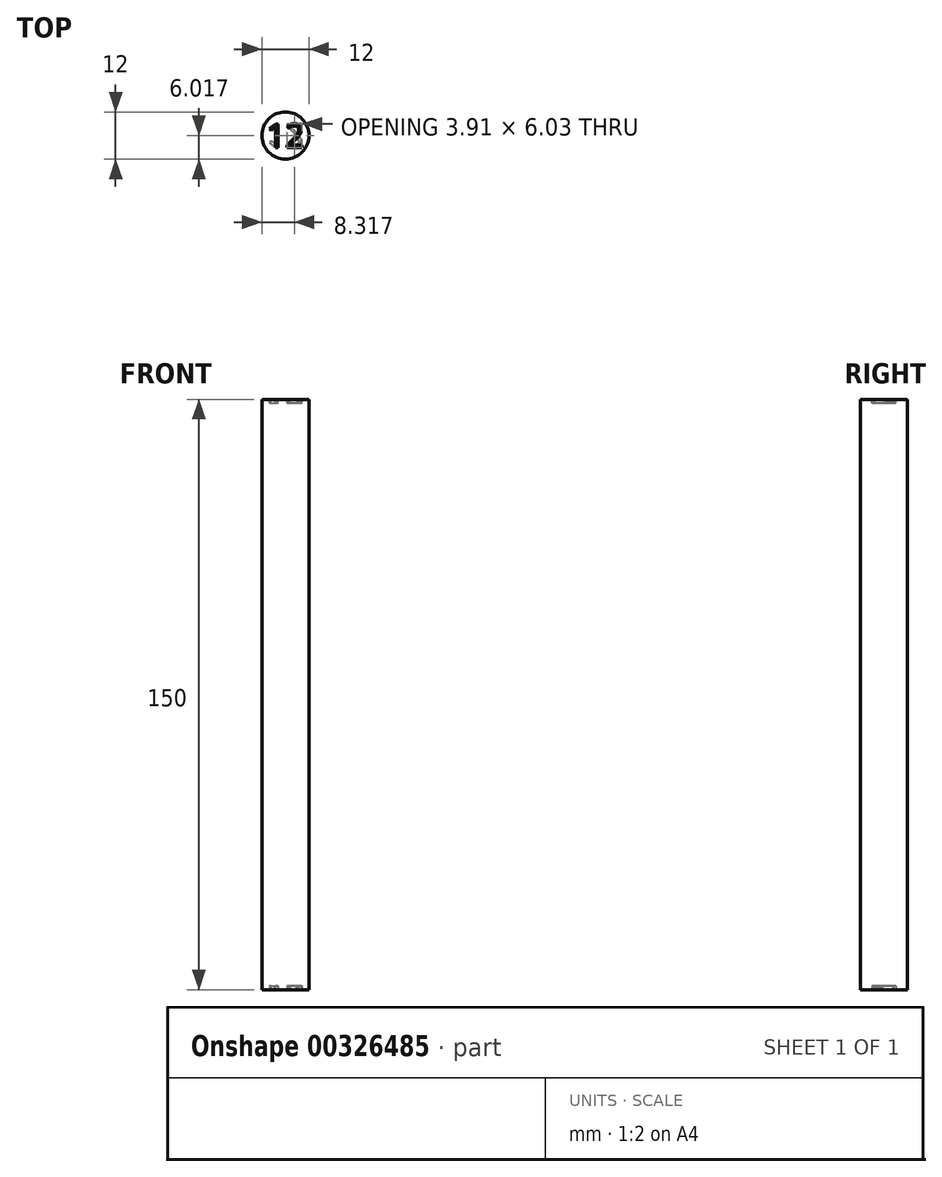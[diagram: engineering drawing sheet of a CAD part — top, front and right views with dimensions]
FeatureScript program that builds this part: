
annotation { "Feature Type Name" : "Feature", "Feature Type Description" : "" }
export const myFeature = defineFeature(function(context is Context, id is Id, definition is map)
    precondition{}
    {
        {
            var Q0;
            Q0=qCreatedBy(makeId("Top.planeOp"),FACE);
            var sketch = newSketch(context, id + "F0", { "sketchPlane" : qUnion([Q0])});
            skCircle(sketch, "E0", {"center": v(0, 0) * mm, "radius": 6 * mm});
            skSolve(sketch);
        }
        {
            var Q0;
            Q0=makeQuery(id+"F0.imprint","IMPRINT",FACE,{"disambiguationData":[TD([[makeQuery(id+"F0.imprint","IMPRINT",EDGE,{"derivedFrom":sQuery(id+"F0.wireOp",EDGE,"E0")}),1.0]])]});
            extrude(context, id + "F1", {"entities" : qUnion([Q0]), "depth" : 150 * mm});
        }
        {
            var Q0;
            Q0=makeQuery(id+"F1.opExtrude","CAP_FACE",FACE,{"disambiguationData":[OSD([sQuery(id+"F0.wireOp",EDGE,"E0")])],"isStart":true});
            var sketch = newSketch(context, id + "F2", { "sketchPlane" : qUnion([Q0])});
            skText(sketch, "E1", { "text": "12", "fontName": "OpenSans-Regular.ttf"});
            const initialGuessF2  = {"E1": [-0.00481, -0.003, 1, 0, 0.006]};
            skSetInitialGuess(sketch, initialGuessF2);
            skSolve(sketch);
        }
        {
            var Q0;
            Q0 = qSketchRegion(id + "F2", true);
            extrude(context, id + "F3", {"entities" : qUnion([Q0]), "operationType" : NewBodyOperationType.REMOVE, "oppositeDirection" : true, "depth" : 1 * mm});
        }
        {
            var Q0;
            Q0=makeQuery(id+"F1.opExtrude","CAP_FACE",FACE,{"disambiguationData":[OSD([sQuery(id+"F0.wireOp",EDGE,"E0")])],"isStart":false});
            var sketch = newSketch(context, id + "F4", { "sketchPlane" : qUnion([Q0])});
            skText(sketch, "E2", { "text": "12", "fontName": "OpenSans-Regular.ttf"});
            const initialGuessF4  = {"E2": [-0.00481, -0.003, 1, 0, 0.006]};
            skSetInitialGuess(sketch, initialGuessF4);
            skSolve(sketch);
        }
        {
            var Q0;
            Q0 = qSketchRegion(id + "F4", true);
            extrude(context, id + "F5", {"entities" : qUnion([Q0]), "operationType" : NewBodyOperationType.REMOVE, "oppositeDirection" : true, "depth" : 1 * mm});
        }
    });
